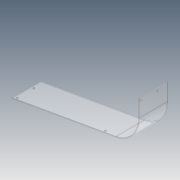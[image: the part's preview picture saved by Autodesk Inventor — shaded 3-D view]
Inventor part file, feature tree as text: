
AUTODESK INVENTOR PART (.ipt)
format: ipt  version: 2012 (Build 160160000, 160)  size: 91,648 bytes
history: native  units: in
note: dims shown in document units (in); Inventor stores cm internally (conversion verified against a paired STEP export)
features: pattern_linear x3, hole x2, extrude x1, sketch x1, reference x1
ambient origin geometry x8: Origin, YZ Plane, XZ Plane, XY Plane, X Axis, Y Axis, Z Axis, Center Point
bodies: Solid1 (feature_tree)
feature tree (8):
  extrude  "Extrusion1"  Depth=0.7874in
  hole  "Hole1"  [1 undecoded]
  pattern_linear  "Rectangular Pattern1"  Count1=2 Spacing1=14.5in
  hole  "Hole2"  [1 undecoded]
  pattern_linear  "Rectangular Pattern2"  [2 undecoded]
  pattern_linear  "Rectangular Pattern3"  [2 undecoded]
  sketch  "Sketch1"  dims[d0=4.625in d1=0.0in d2=0.3125in d3=0.5in d4=0.265in d5=0.75in d6=0.375in d7=0.25in d8=0.5635in d9=1.0in d10=0.8108in d11=0.7874in d13=2.6875in d14=0.5in d15=0.3125in d16=0.265in d17=0.75in d18=0.375in d19=0.25in d20=0.5635in d21=1.0in d22=0.8108in d23=0.7874in d25=2.6875in d26=0.7874in d28=14.5in]
  reference  "Reference1"
note: 6 required parameter values undecoded (feature->parameter linkage not recoverable at this tier; creation-order binding heuristic only, values carry confidence <= 0.55)
